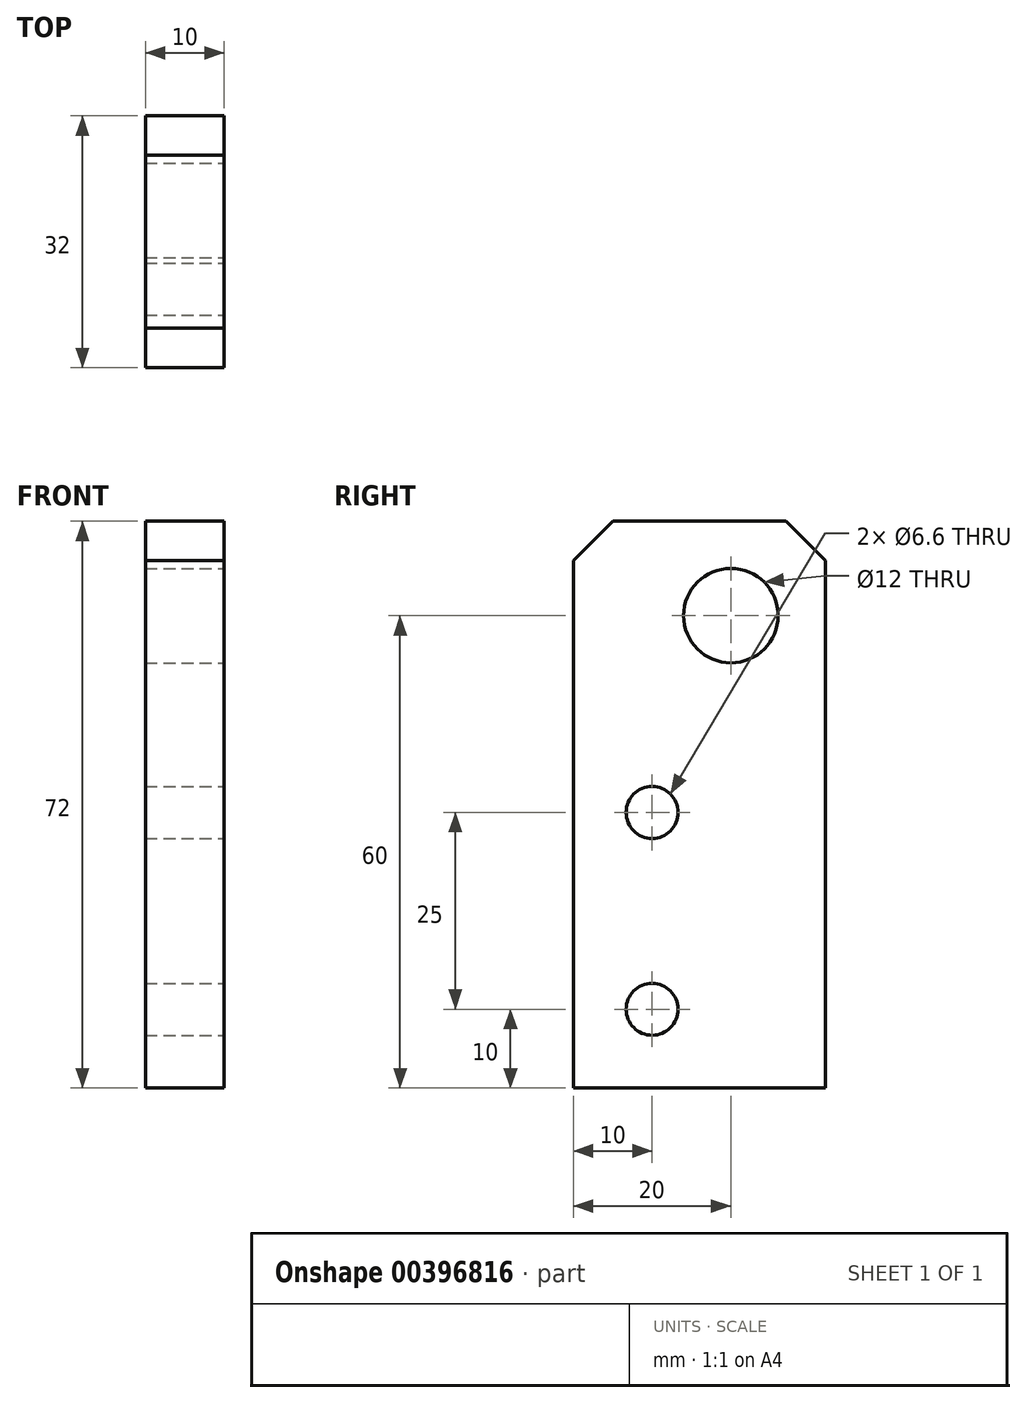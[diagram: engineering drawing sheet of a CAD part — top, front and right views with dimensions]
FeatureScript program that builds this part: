
annotation { "Feature Type Name" : "Feature", "Feature Type Description" : "" }
export const myFeature = defineFeature(function(context is Context, id is Id, definition is map)
    precondition{}
    {
        {
            var Q0;
            Q0=qCreatedBy(makeId("Right.planeOp"),FACE);
            var sketch = newSketch(context, id + "F0", { "sketchPlane" : qUnion([Q0])});
            skLineSegment(sketch, "E0.bottom", {"start": v(0, 0) * mm, "end": v(32, 0) * mm});
            skLineSegment(sketch, "E0.top", {"start": v(0, 72) * mm, "end": v(32, 72) * mm});
            skLineSegment(sketch, "E0.left", {"start": v(0, 0) * mm, "end": v(0, 72) * mm});
            skLineSegment(sketch, "E0.right", {"start": v(32, 0) * mm, "end": v(32, 72) * mm});
            skSolve(sketch);
        }
        {
            var Q0;
            Q0 = qSketchRegion(id + "F0", true);
            extrude(context, id + "F1", {"entities" : qUnion([Q0]), "depth" : 10 * mm});
        }
        {
            var Q0;
            Q0=makeQuery(id+"F1.opExtrude","CAP_FACE",FACE,{"disambiguationData":[OSD([sQuery(id+"F0.wireOp",EDGE,"E0.bottom"),sQuery(id+"F0.wireOp",EDGE,"E0.top"),sQuery(id+"F0.wireOp",EDGE,"E0.left"),sQuery(id+"F0.wireOp",EDGE,"E0.right")])],"isStart":false});
            var sketch = newSketch(context, id + "F2", { "sketchPlane" : qUnion([Q0])});
            skPoint(sketch, "E1", {"position": v(10, 10) * mm});
            skPoint(sketch, "E2", {"position": v(10, 35) * mm});
            skSolve(sketch);
        }
        {
            var Q0;
            Q0=sQuery(id+"F2.wireOp",VERTEX,"E2");
            var Q1;
            Q1=sQuery(id+"F2.wireOp",VERTEX,"E1");
            var Q2;
            Q2=makeQuery(id+"F1.opExtrude","SWEPT_BODY",BODY,{"disambiguationData":[OSD([sQuery(id+"F0.wireOp",EDGE,"E0.bottom"),sQuery(id+"F0.wireOp",EDGE,"E0.top"),sQuery(id+"F0.wireOp",EDGE,"E0.left"),sQuery(id+"F0.wireOp",EDGE,"E0.right")])]});
            hole(context, id + "F3", {"style" : HoleStyle.SIMPLE, "endStyle" : HoleEndStyle.THROUGH, "standardTappedOrClearance" : lookupTablePath({ "standard" : "ISO", "size" : "6.6", "type" : "Drilled" }), "standardBlindInLast" : lookupTablePath({ "standard" : "ISO", "size" : "6.6", "type" : "Drilled" }), "holeDiameter" : 6.6 * mm, "isTappedThrough" : true, "tappedDepth" : 12 * mm, "tapClearance" : 3, "locations" : qUnion([Q0, Q1]), "scope" : qUnion([Q2])});
        }
        {
            var Q0;
            Q0=makeQuery(id+"F1.opExtrude","CAP_FACE",FACE,{"disambiguationData":[OSD([sQuery(id+"F0.wireOp",EDGE,"E0.bottom"),sQuery(id+"F0.wireOp",EDGE,"E0.top"),sQuery(id+"F0.wireOp",EDGE,"E0.left"),sQuery(id+"F0.wireOp",EDGE,"E0.right")])],"isStart":false});
            var sketch = newSketch(context, id + "F4", { "sketchPlane" : qUnion([Q0])});
            skPoint(sketch, "E3", {"position": v(20, 60) * mm});
            skSolve(sketch);
        }
        {
            var Q0;
            Q0=sQuery(id+"F4.wireOp",VERTEX,"E3");
            var Q1;
            Q1=makeQuery(id+"F1.opExtrude","SWEPT_BODY",BODY,{"disambiguationData":[OSD([sQuery(id+"F0.wireOp",EDGE,"E0.bottom"),sQuery(id+"F0.wireOp",EDGE,"E0.top"),sQuery(id+"F0.wireOp",EDGE,"E0.left"),sQuery(id+"F0.wireOp",EDGE,"E0.right")])]});
            hole(context, id + "F5", {"style" : HoleStyle.SIMPLE, "endStyle" : HoleEndStyle.THROUGH, "standardTappedOrClearance" : lookupTablePath({ "standard" : "ISO", "size" : "12", "type" : "Drilled" }), "standardBlindInLast" : lookupTablePath({ "standard" : "ISO", "size" : "12", "type" : "Drilled" }), "holeDiameter" : 12 * mm, "isTappedThrough" : true, "tappedDepth" : 12 * mm, "tapClearance" : 3, "locations" : qUnion([Q0]), "scope" : qUnion([Q1])});
        }
        {
            var Q0;
            Q0=makeQuery(id+"F1.opExtrude","SWEPT_EDGE",EDGE,{"disambiguationData":[OSD([sQuery(id+"F0.wireOp",EDGE,"E0.top"),sQuery(id+"F0.wireOp",EDGE,"E0.left")])]});
            var Q1;
            Q1=makeQuery(id+"F1.opExtrude","SWEPT_EDGE",EDGE,{"disambiguationData":[OSD([sQuery(id+"F0.wireOp",EDGE,"E0.top"),sQuery(id+"F0.wireOp",EDGE,"E0.right")])]});
            chamfer(context, id + "F6", {"entities" : qUnion([Q0, Q1]), "width" : 5 * mm, "tangentPropagation" : true});
        }
    });
